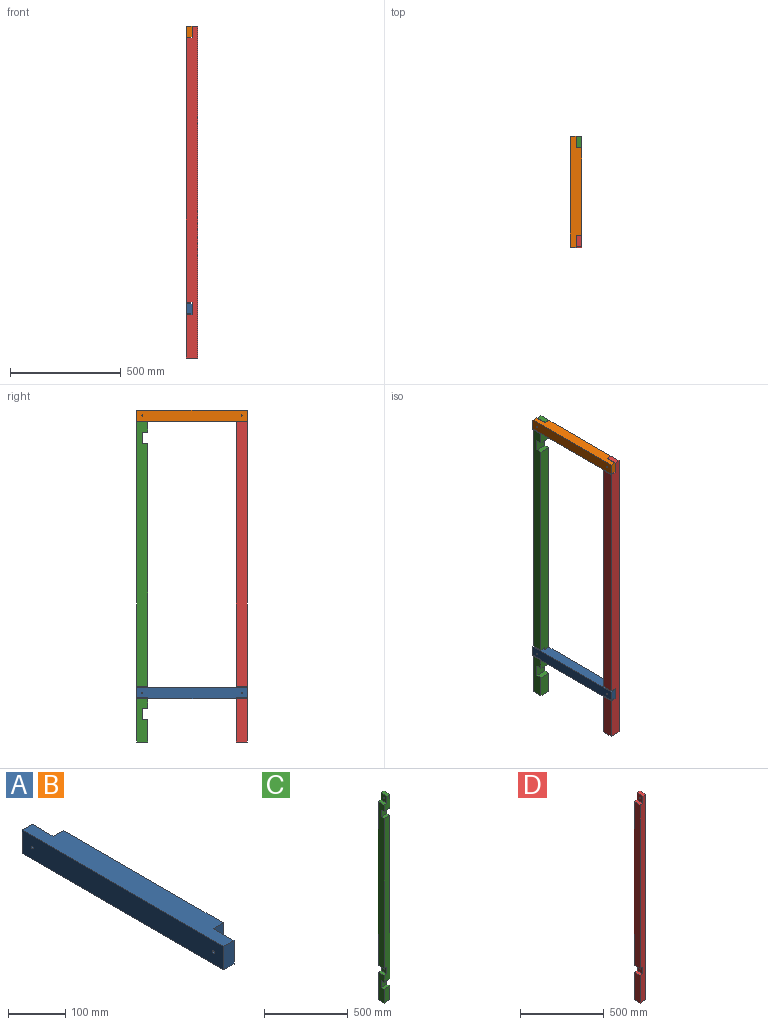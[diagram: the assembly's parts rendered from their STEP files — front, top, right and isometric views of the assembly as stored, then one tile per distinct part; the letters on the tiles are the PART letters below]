
ASSEMBLY  parts=4 mates=3
PART A: 12 faces, bbox 50x500x50 mm
  f0: plane 500x50mm, normal (0,0,-1), area 22400mm2, adj f1,f2,f3,f5,f6,f7,f8,f9
  f1: plane 396x50mm, normal (1,0,0), area 19800mm2, adj f0,f4,f7,f9
  f2: plane 50x25mm, normal (0,1,0), area 1250mm2, adj f0,f4,f5,f8
  f3: plane 50x25mm, normal (0,-1,0), area 1250mm2, adj f0,f4,f5,f6
  f4: plane 500x50mm, normal (0,0,1), area 22400mm2, adj f1,f2,f3,f5,f6,f7,f8,f9
  f5: plane 500x50mm, normal (-1,0,0), area 24960.7mm2, adj f0,f2,f3,f4,f10,f11
  f6: plane 52x50mm, normal (1,0,0), area 2580.4mm2, adj f0,f3,f4,f7,f10
  f7: plane 50x25mm, normal (0,-1,0), area 1250mm2, adj f0,f1,f4,f6
  f8: plane 52x50mm, normal (1,0,0), area 2580.4mm2, adj f0,f2,f4,f9,f11
  f9: plane 50x25mm, normal (0,1,0), area 1250mm2, adj f0,f1,f4,f8
  f10: cylinder r=2.5mm len=25mm, axis (1,0,0), area 392.7mm2, adj f5,f6
  f11: cylinder r=2.5mm len=25mm, axis (1,0,0), area 392.7mm2, adj f5,f8
PART B: same geometry as A
PART C: 23 faces, bbox 50x50x1500 mm
  f0: plane 1196x50mm, normal (0,-1,0), area 58500mm2, adj f2,f3,f5,f12,f13,f14,f16,f20
  f1: plane 100x50mm, normal (0,-1,0), area 5000mm2, adj f2,f3,f8,f17
  f2: plane 1500x50mm, normal (1,0,0), area 72360.7mm2, adj f0,f1,f4,f6,f7,f8,f11,f15
  f3: plane 200x50mm, normal (-1,0,0), area 8700mm2, adj f0,f1,f4,f8,f13,f16,f17,f18
  f4: plane 1500x50mm, normal (0,1,0), area 72392.9mm2, adj f2,f3,f5,f6,f8,f9,f10,f12
  f5: plane 1196x50mm, normal (-1,0,0), area 58500mm2, adj f0,f4,f7,f9,f12,f19,f20,f21
  f6: plane 50x25mm, normal (0,0,1), area 1250mm2, adj f2,f4,f7,f10
  f7: plane 100x50mm, normal (0,-1,0), area 3700mm2, adj f2,f5,f6,f9,f10,f19
  f8: plane 50x50mm, normal (0,0,-1), area 2500mm2, adj f1,f2,f3,f4
  f9: plane 50x25mm, normal (0,0,1), area 1250mm2, adj f4,f5,f7,f10
  f10: plane 52x50mm, normal (-1,0,0), area 2580.4mm2, adj f4,f6,f7,f9,f11
  f11: cylinder r=2.5mm len=25mm, axis (-1,0,0), area 392.7mm2, adj f2,f10
  f12: plane 50x25mm, normal (0,0,-1), area 1250mm2, adj f0,f4,f5,f14
  f13: plane 50x25mm, normal (0,0,1), area 1250mm2, adj f0,f3,f4,f14
  f14: plane 52x50mm, normal (-1,0,0), area 2580.4mm2, adj f0,f4,f12,f13,f15
  f15: cylinder r=2.5mm len=25mm, axis (-1,0,0), area 392.7mm2, adj f2,f14
  f16: plane 50x25mm, normal (0,0,-1), area 1250mm2, adj f0,f2,f3,f18
  f17: plane 50x25mm, normal (0,0,1), area 1250mm2, adj f1,f2,f3,f18
  f18: plane 52x50mm, normal (0,-1,0), area 2592.9mm2, adj f2,f3,f16,f17,f22
  f19: plane 50x25mm, normal (0,0,-1), area 1250mm2, adj f2,f5,f7,f21
  f20: plane 50x25mm, normal (0,0,1), area 1250mm2, adj f0,f2,f5,f21
  f21: plane 52x50mm, normal (0,-1,0), area 2600mm2, adj f2,f5,f19,f20
  f22: cylinder r=1.5mm len=25mm, axis (0,-1,0), area 235.6mm2, adj f4,f18
PART D: 14 faces, bbox 50x50x1500 mm
  f0: plane 200x50mm, normal (-1,0,0), area 10000mm2, adj f1,f4,f5,f11
  f1: plane 1500x50mm, normal (0,1,0), area 72400mm2, adj f0,f2,f3,f5,f6,f7,f8,f10
  f2: plane 1196x50mm, normal (-1,0,0), area 59800mm2, adj f1,f4,f7,f10
  f3: plane 50x25mm, normal (0,0,1), area 1250mm2, adj f1,f4,f6,f8
  f4: plane 1500x50mm, normal (0,-1,0), area 72400mm2, adj f0,f2,f3,f5,f6,f7,f8,f10
  f5: plane 50x50mm, normal (0,0,-1), area 2500mm2, adj f0,f1,f4,f6
  f6: plane 1500x50mm, normal (1,0,0), area 74960.7mm2, adj f1,f3,f4,f5,f9,f13
  f7: plane 50x25mm, normal (0,0,1), area 1250mm2, adj f1,f2,f4,f8
  f8: plane 52x50mm, normal (-1,0,0), area 2580.4mm2, adj f1,f3,f4,f7,f9
  f9: cylinder r=2.5mm len=25mm, axis (-1,0,0), area 392.7mm2, adj f6,f8
  f10: plane 50x25mm, normal (0,0,-1), area 1250mm2, adj f1,f2,f4,f12
  f11: plane 50x25mm, normal (0,0,1), area 1250mm2, adj f0,f1,f4,f12
  f12: plane 52x50mm, normal (-1,0,0), area 2580.4mm2, adj f1,f4,f10,f11,f13
  f13: cylinder r=2.5mm len=25mm, axis (-1,0,0), area 392.7mm2, adj f6,f12
PLACE A t=(239.4,-303.19,-999.06)mm
PLACE B t=(239.4,-303.19,255.94)mm
PLACE C t=(14.4,-303.69,255.94)mm
PLACE D t=(214.4,-752.69,255.94)mm
MATE fastened C.f15 <-> A.f11  axis (-1,0,0) through (65.15,157.24,-1018.06)mm
MATE fastened A.f10 <-> D.f13  axis (1,0,0) through (65.15,-291.26,-1024.06)mm
MATE fastened B.f10 <-> D.f9  axis (1,0,0) through (65.15,-291.26,230.94)mm
